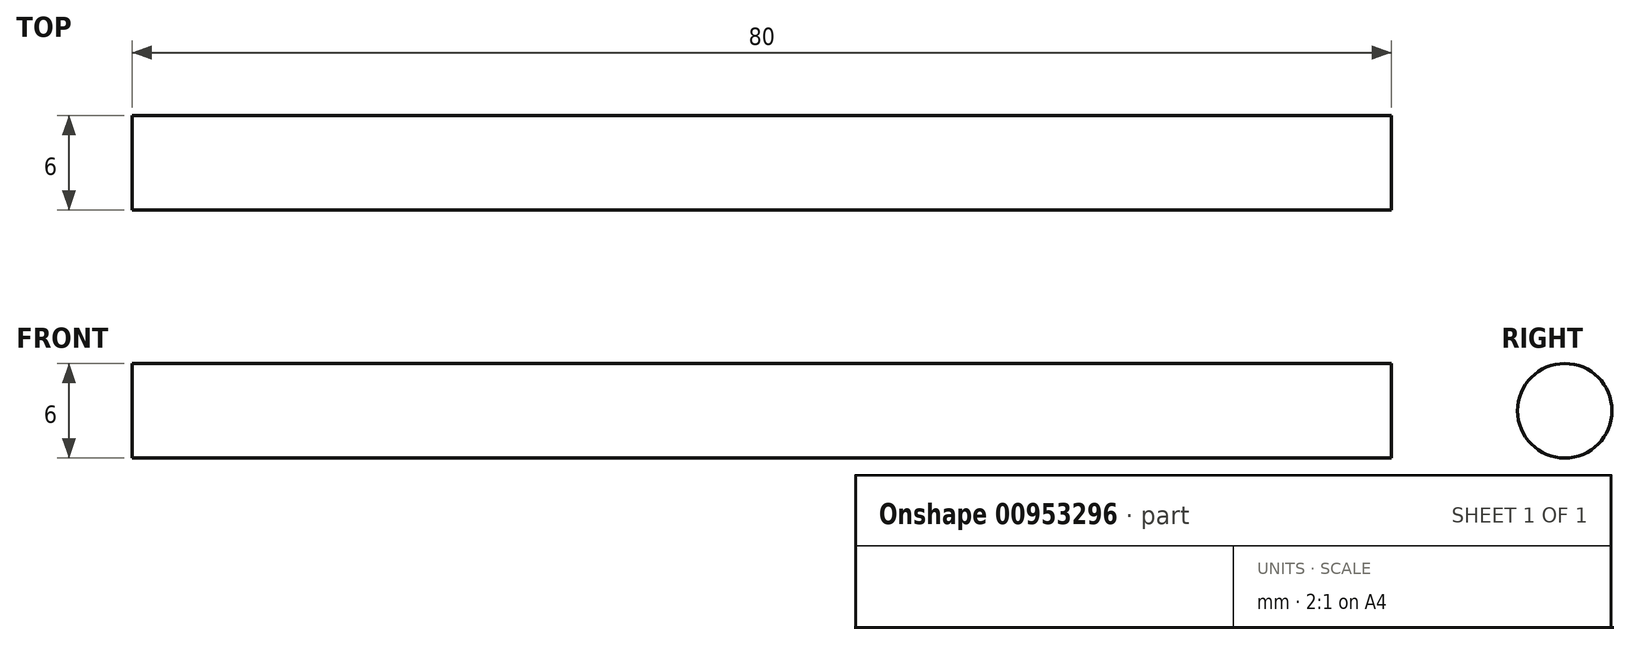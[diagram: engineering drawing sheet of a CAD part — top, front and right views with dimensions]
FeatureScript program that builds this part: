
annotation { "Feature Type Name" : "Feature", "Feature Type Description" : "" }
export const myFeature = defineFeature(function(context is Context, id is Id, definition is map)
    precondition{}
    {
        {
            var Q0;
            Q0=qCreatedBy(makeId("Right.planeOp"),FACE);
            var sketch = newSketch(context, id + "F0", { "sketchPlane" : qUnion([Q0])});
            skCircle(sketch, "E0", {"center": v(0, 0) * mm, "radius": 3 * mm});
            skSolve(sketch);
        }
        {
            var Q0;
            Q0 = qSketchRegion(id + "F0", true);
            extrude(context, id + "F1", {"entities" : qUnion([Q0]), "depth" : 80 * mm, "offsetDistance" : 25 * mm});
        }
    });
